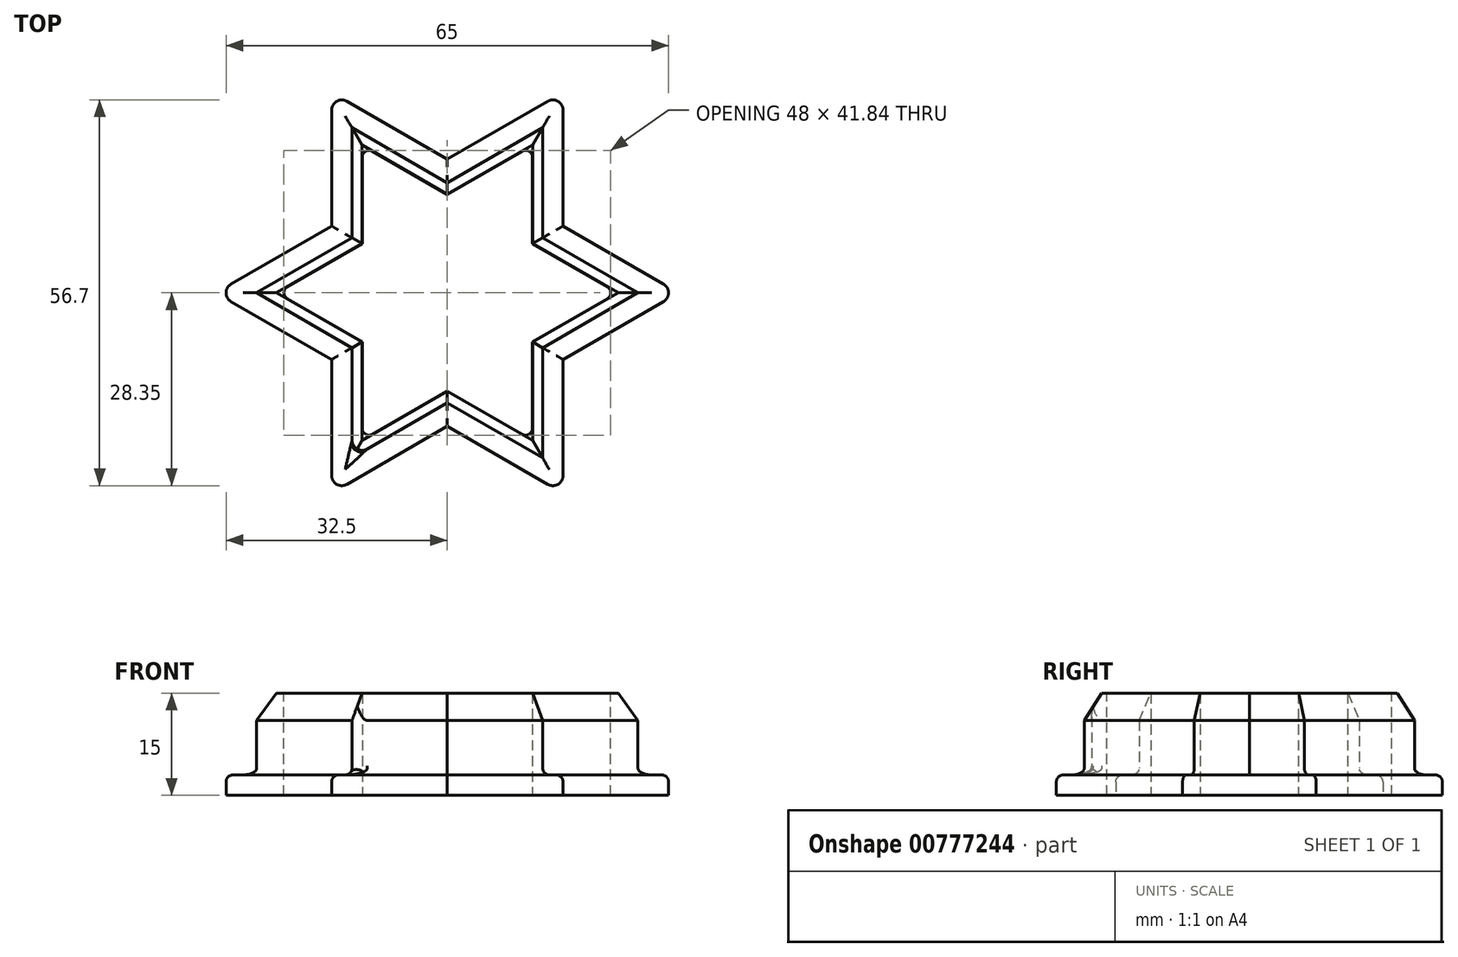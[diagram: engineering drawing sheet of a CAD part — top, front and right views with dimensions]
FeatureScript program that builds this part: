
annotation { "Feature Type Name" : "Feature", "Feature Type Description" : "" }
export const myFeature = defineFeature(function(context is Context, id is Id, definition is map)
    precondition{}
    {
        {
            var Q0;
            Q0=qCreatedBy(makeId("Top.planeOp"),FACE);
            var sketch = newSketch(context, id + "F0", { "sketchPlane" : qUnion([Q0])});
            skCircle(sketch, "E0.cCircle", {"center": v(0, 0) * mm, "radius": 25 * mm, "construction": true});
            skPoint(sketch, "E0.0.midPoint", {"position": v(-25, 0) * mm});
            skLineSegment(sketch, "E1", {"start": v(-25, 0) * mm, "end": v(-12.5, 7.22) * mm});
            skLineSegment(sketch, "E2", {"start": v(12.5, 21.65) * mm, "end": v(12.5, 7.22) * mm});
            skLineSegment(sketch, "E3", {"start": v(12.5, -21.65) * mm, "end": v(0, -14.43) * mm});
            skLineSegment(sketch, "E4", {"start": v(-12.5, -21.65) * mm, "end": v(-12.5, -7.22) * mm});
            skLineSegment(sketch, "E5", {"start": v(-12.5, 21.65) * mm, "end": v(0, 14.43) * mm});
            skLineSegment(sketch, "E6", {"start": v(25, 0) * mm, "end": v(12.5, -7.22) * mm});
            skPoint(sketch, "E7.orphan", {"position": v(-25, 14.43) * mm});
            skPoint(sketch, "E0.0.start.orphan", {"position": v(-25, -14.43) * mm});
            skPoint(sketch, "E8.orphan", {"position": v(0, -28.87) * mm});
            skPoint(sketch, "E9.orphan", {"position": v(25, -14.43) * mm});
            skPoint(sketch, "E10.orphan", {"position": v(25, 14.43) * mm});
            skPoint(sketch, "E0.1.end.orphan", {"position": v(0, 28.87) * mm});
            skLineSegment(sketch, "E11", {"start": v(-12.5, 7.22) * mm, "end": v(-12.5, 21.65) * mm});
            skLineSegment(sketch, "E12", {"start": v(0, 14.43) * mm, "end": v(12.5, 21.65) * mm});
            skLineSegment(sketch, "E13", {"start": v(12.5, 7.22) * mm, "end": v(25, 0) * mm});
            skLineSegment(sketch, "E14", {"start": v(12.5, -7.22) * mm, "end": v(12.5, -21.65) * mm});
            skLineSegment(sketch, "E15", {"start": v(-12.5, -7.22) * mm, "end": v(-25, 0) * mm});
            skLineSegment(sketch, "E16.trimOffspring", {"start": v(0, -14.43) * mm, "end": v(-12.5, -21.65) * mm});
            skLineSegment(sketch, "E17.0", {"start": v(-14, -24.25) * mm, "end": v(-14, -8.08) * mm});
            skLineSegment(sketch, "E17.1", {"start": v(0, 16.17) * mm, "end": v(14, 24.25) * mm});
            skLineSegment(sketch, "E17.2", {"start": v(-14, 24.25) * mm, "end": v(0, 16.17) * mm});
            skLineSegment(sketch, "E17.3", {"start": v(-14, 8.08) * mm, "end": v(-14, 24.25) * mm});
            skLineSegment(sketch, "E17.4", {"start": v(-28, 0) * mm, "end": v(-14, 8.08) * mm});
            skLineSegment(sketch, "E17.5", {"start": v(14, 24.25) * mm, "end": v(14, 8.08) * mm});
            skLineSegment(sketch, "E17.6", {"start": v(-14, -8.08) * mm, "end": v(-28, 0) * mm});
            skLineSegment(sketch, "E17.7", {"start": v(14, 8.08) * mm, "end": v(28, 0) * mm});
            skLineSegment(sketch, "E17.8", {"start": v(28, 0) * mm, "end": v(14, -8.08) * mm});
            skLineSegment(sketch, "E17.9", {"start": v(14, -8.08) * mm, "end": v(14, -24.25) * mm});
            skLineSegment(sketch, "E17.10", {"start": v(14, -24.25) * mm, "end": v(0, -16.17) * mm});
            skLineSegment(sketch, "E17.11", {"start": v(0, -16.17) * mm, "end": v(-14, -24.25) * mm});
            skLineSegment(sketch, "E18.0", {"start": v(-17, -29.44) * mm, "end": v(-17, -9.81) * mm});
            skLineSegment(sketch, "E18.1", {"start": v(0, 19.63) * mm, "end": v(17, 29.44) * mm});
            skLineSegment(sketch, "E18.2", {"start": v(-17, 29.44) * mm, "end": v(0, 19.63) * mm});
            skLineSegment(sketch, "E18.3", {"start": v(-17, 9.81) * mm, "end": v(-17, 29.44) * mm});
            skLineSegment(sketch, "E18.4", {"start": v(-34, 0) * mm, "end": v(-17, 9.81) * mm});
            skLineSegment(sketch, "E18.5", {"start": v(17, 29.44) * mm, "end": v(17, 9.81) * mm});
            skLineSegment(sketch, "E18.6", {"start": v(-17, -9.81) * mm, "end": v(-34, 0) * mm});
            skLineSegment(sketch, "E18.7", {"start": v(17, 9.81) * mm, "end": v(34, 0) * mm});
            skLineSegment(sketch, "E18.8", {"start": v(34, 0) * mm, "end": v(17, -9.81) * mm});
            skLineSegment(sketch, "E18.9", {"start": v(17, -9.81) * mm, "end": v(17, -29.44) * mm});
            skLineSegment(sketch, "E18.10", {"start": v(17, -29.44) * mm, "end": v(0, -19.63) * mm});
            skLineSegment(sketch, "E18.11", {"start": v(0, -19.63) * mm, "end": v(-17, -29.44) * mm});
            skSolve(sketch);
        }
        {
            var Q0;
            Q0=makeQuery(id+"F0.imprint","IMPRINT",FACE,{"disambiguationData":[TD([[makeQuery(id+"F0.imprint","IMPRINT",EDGE,{"derivedFrom":sQuery(id+"F0.wireOp",EDGE,"E17.0")}),1.0]])]});
            extrude(context, id + "F1", {"entities" : qUnion([Q0]), "depth" : 3 * mm, "offsetDistance" : 25 * mm});
        }
        {
            var Q0;
            Q0=makeQuery(id+"F0.imprint","IMPRINT",FACE,{"disambiguationData":[TD([[makeQuery(id+"F0.imprint","IMPRINT",EDGE,{"derivedFrom":sQuery(id+"F0.wireOp",EDGE,"E1")}),1.0]])]});
            extrude(context, id + "F2", {"entities" : qUnion([Q0]), "operationType" : NewBodyOperationType.ADD, "depth" : 15 * mm, "offsetDistance" : 25 * mm});
        }
        {
            var Q0;
            Q0=makeQuery(id+"F2.opExtrude","CAP_EDGE",EDGE,{"disambiguationData":[OSD([sQuery(id+"F0.wireOp",EDGE,"E17.11")])],"isStart":false});
            var Q1;
            Q1=makeQuery(id+"F2.opExtrude","CAP_EDGE",EDGE,{"disambiguationData":[OSD([sQuery(id+"F0.wireOp",EDGE,"E17.10")])],"isStart":false});
            var Q2;
            Q2=makeQuery(id+"F2.opExtrude","CAP_EDGE",EDGE,{"disambiguationData":[OSD([sQuery(id+"F0.wireOp",EDGE,"E17.9")])],"isStart":false});
            var Q3;
            Q3=makeQuery(id+"F2.opExtrude","CAP_EDGE",EDGE,{"disambiguationData":[OSD([sQuery(id+"F0.wireOp",EDGE,"E17.8")])],"isStart":false});
            var Q4;
            Q4=makeQuery(id+"F2.opExtrude","CAP_EDGE",EDGE,{"disambiguationData":[OSD([sQuery(id+"F0.wireOp",EDGE,"E17.0")])],"isStart":false});
            var Q5;
            Q5=makeQuery(id+"F2.opExtrude","CAP_EDGE",EDGE,{"disambiguationData":[OSD([sQuery(id+"F0.wireOp",EDGE,"E17.6")])],"isStart":false});
            var Q6;
            Q6=makeQuery(id+"F2.opExtrude","CAP_EDGE",EDGE,{"disambiguationData":[OSD([sQuery(id+"F0.wireOp",EDGE,"E17.4")])],"isStart":false});
            var Q7;
            Q7=makeQuery(id+"F2.opExtrude","CAP_EDGE",EDGE,{"disambiguationData":[OSD([sQuery(id+"F0.wireOp",EDGE,"E17.3")])],"isStart":false});
            var Q8;
            Q8=makeQuery(id+"F2.opExtrude","CAP_EDGE",EDGE,{"disambiguationData":[OSD([sQuery(id+"F0.wireOp",EDGE,"E17.2")])],"isStart":false});
            var Q9;
            Q9=makeQuery(id+"F2.opExtrude","CAP_EDGE",EDGE,{"disambiguationData":[OSD([sQuery(id+"F0.wireOp",EDGE,"E17.1")])],"isStart":false});
            var Q10;
            Q10=makeQuery(id+"F2.opExtrude","CAP_EDGE",EDGE,{"disambiguationData":[OSD([sQuery(id+"F0.wireOp",EDGE,"E17.5")])],"isStart":false});
            var Q11;
            Q11=makeQuery(id+"F2.opExtrude","CAP_EDGE",EDGE,{"disambiguationData":[OSD([sQuery(id+"F0.wireOp",EDGE,"E17.7")])],"isStart":false});
            chamfer(context, id + "F3", {"entities" : qUnion([Q0, Q1, Q2, Q3, Q4, Q5, Q6, Q7, Q8, Q9, Q10, Q11]), "chamferType" : ChamferType.OFFSET_ANGLE, "width" : 4 * mm, "oppositeDirection" : false, "angle" : 20 * degree, "tangentPropagation" : true});
        }
        {
            var Q0;
            Q0=makeQuery(id+"F1.opExtrude","CAP_FACE",FACE,{"disambiguationData":[OSD([sQuery(id+"F0.wireOp",EDGE,"E17.0"),sQuery(id+"F0.wireOp",EDGE,"E17.1"),sQuery(id+"F0.wireOp",EDGE,"E17.2"),sQuery(id+"F0.wireOp",EDGE,"E17.3"),sQuery(id+"F0.wireOp",EDGE,"E17.4"),sQuery(id+"F0.wireOp",EDGE,"E17.5"),sQuery(id+"F0.wireOp",EDGE,"E17.6"),sQuery(id+"F0.wireOp",EDGE,"E17.7"),sQuery(id+"F0.wireOp",EDGE,"E17.8"),sQuery(id+"F0.wireOp",EDGE,"E17.9"),sQuery(id+"F0.wireOp",EDGE,"E17.10"),sQuery(id+"F0.wireOp",EDGE,"E17.11"),sQuery(id+"F0.wireOp",EDGE,"E18.0"),sQuery(id+"F0.wireOp",EDGE,"E18.1"),sQuery(id+"F0.wireOp",EDGE,"E18.2"),sQuery(id+"F0.wireOp",EDGE,"E18.3"),sQuery(id+"F0.wireOp",EDGE,"E18.4"),sQuery(id+"F0.wireOp",EDGE,"E18.5"),sQuery(id+"F0.wireOp",EDGE,"E18.6"),sQuery(id+"F0.wireOp",EDGE,"E18.7"),sQuery(id+"F0.wireOp",EDGE,"E18.8"),sQuery(id+"F0.wireOp",EDGE,"E18.9"),sQuery(id+"F0.wireOp",EDGE,"E18.10"),sQuery(id+"F0.wireOp",EDGE,"E18.11")])],"isStart":false});
            fillet(context, id + "F4", {"entities" : qUnion([Q0]), "radius" : 1 * mm, "tangentPropagation" : true, "allowEdgeOverflow" : false});
        }
        {
            var Q0;
            Q0=makeQuery(id+"F1.opExtrude","SWEPT_EDGE",EDGE,{"disambiguationData":[OSD([sQuery(id+"F0.wireOp",EDGE,"E18.9"),sQuery(id+"F0.wireOp",EDGE,"E18.10")])]});
            var Q1;
            Q1=makeQuery(id+"F1.opExtrude","SWEPT_EDGE",EDGE,{"disambiguationData":[OSD([sQuery(id+"F0.wireOp",EDGE,"E18.7"),sQuery(id+"F0.wireOp",EDGE,"E18.8")])]});
            var Q2;
            Q2=makeQuery(id+"F1.opExtrude","SWEPT_EDGE",EDGE,{"disambiguationData":[OSD([sQuery(id+"F0.wireOp",EDGE,"E18.1"),sQuery(id+"F0.wireOp",EDGE,"E18.5")])]});
            var Q3;
            Q3=makeQuery(id+"F1.opExtrude","SWEPT_EDGE",EDGE,{"disambiguationData":[OSD([sQuery(id+"F0.wireOp",EDGE,"E18.2"),sQuery(id+"F0.wireOp",EDGE,"E18.3")])]});
            var Q4;
            Q4=makeQuery(id+"F1.opExtrude","SWEPT_EDGE",EDGE,{"disambiguationData":[OSD([sQuery(id+"F0.wireOp",EDGE,"E18.4"),sQuery(id+"F0.wireOp",EDGE,"E18.6")])]});
            var Q5;
            Q5=makeQuery(id+"F1.opExtrude","SWEPT_EDGE",EDGE,{"disambiguationData":[OSD([sQuery(id+"F0.wireOp",EDGE,"E18.0"),sQuery(id+"F0.wireOp",EDGE,"E18.11")])]});
            var Q6;
            Q6=makeQuery(id+"F2.opExtrude","SWEPT_EDGE",EDGE,{"disambiguationData":[OSD([sQuery(id+"F0.wireOp",EDGE,"E17.0"),sQuery(id+"F0.wireOp",EDGE,"E17.11")])]});
            fillet(context, id + "F5", {"entities" : qUnion([Q0, Q1, Q2, Q3, Q4, Q5, Q6]), "radius" : 1.5 * mm, "tangentPropagation" : true, "allowEdgeOverflow" : false});
        }
        {
            var Q0;
            Q0=makeQuery(id+"F2.opExtrude","SWEPT_EDGE",EDGE,{"disambiguationData":[OSD([sQuery(id+"F0.wireOp",EDGE,"E2"),sQuery(id+"F0.wireOp",EDGE,"E12")])]});
            var Q1;
            Q1=makeQuery(id+"F2.opExtrude","SWEPT_EDGE",EDGE,{"disambiguationData":[OSD([sQuery(id+"F0.wireOp",EDGE,"E5"),sQuery(id+"F0.wireOp",EDGE,"E11")])]});
            var Q2;
            Q2=makeQuery(id+"F2.opExtrude","SWEPT_EDGE",EDGE,{"disambiguationData":[OSD([sQuery(id+"F0.wireOp",EDGE,"E1"),sQuery(id+"F0.wireOp",EDGE,"E15")])]});
            var Q3;
            Q3=makeQuery(id+"F2.opExtrude","SWEPT_EDGE",EDGE,{"disambiguationData":[OSD([sQuery(id+"F0.wireOp",EDGE,"E4"),sQuery(id+"F0.wireOp",EDGE,"E16.trimOffspring")])]});
            var Q4;
            Q4=makeQuery(id+"F2.opExtrude","SWEPT_EDGE",EDGE,{"disambiguationData":[OSD([sQuery(id+"F0.wireOp",EDGE,"E3"),sQuery(id+"F0.wireOp",EDGE,"E14")])]});
            var Q5;
            Q5=makeQuery(id+"F2.opExtrude","SWEPT_EDGE",EDGE,{"disambiguationData":[OSD([sQuery(id+"F0.wireOp",EDGE,"E6"),sQuery(id+"F0.wireOp",EDGE,"E13")])]});
            fillet(context, id + "F6", {"entities" : qUnion([Q0, Q1, Q2, Q3, Q4, Q5]), "radius" : 1 * mm, "tangentPropagation" : true, "allowEdgeOverflow" : false});
        }
    });
